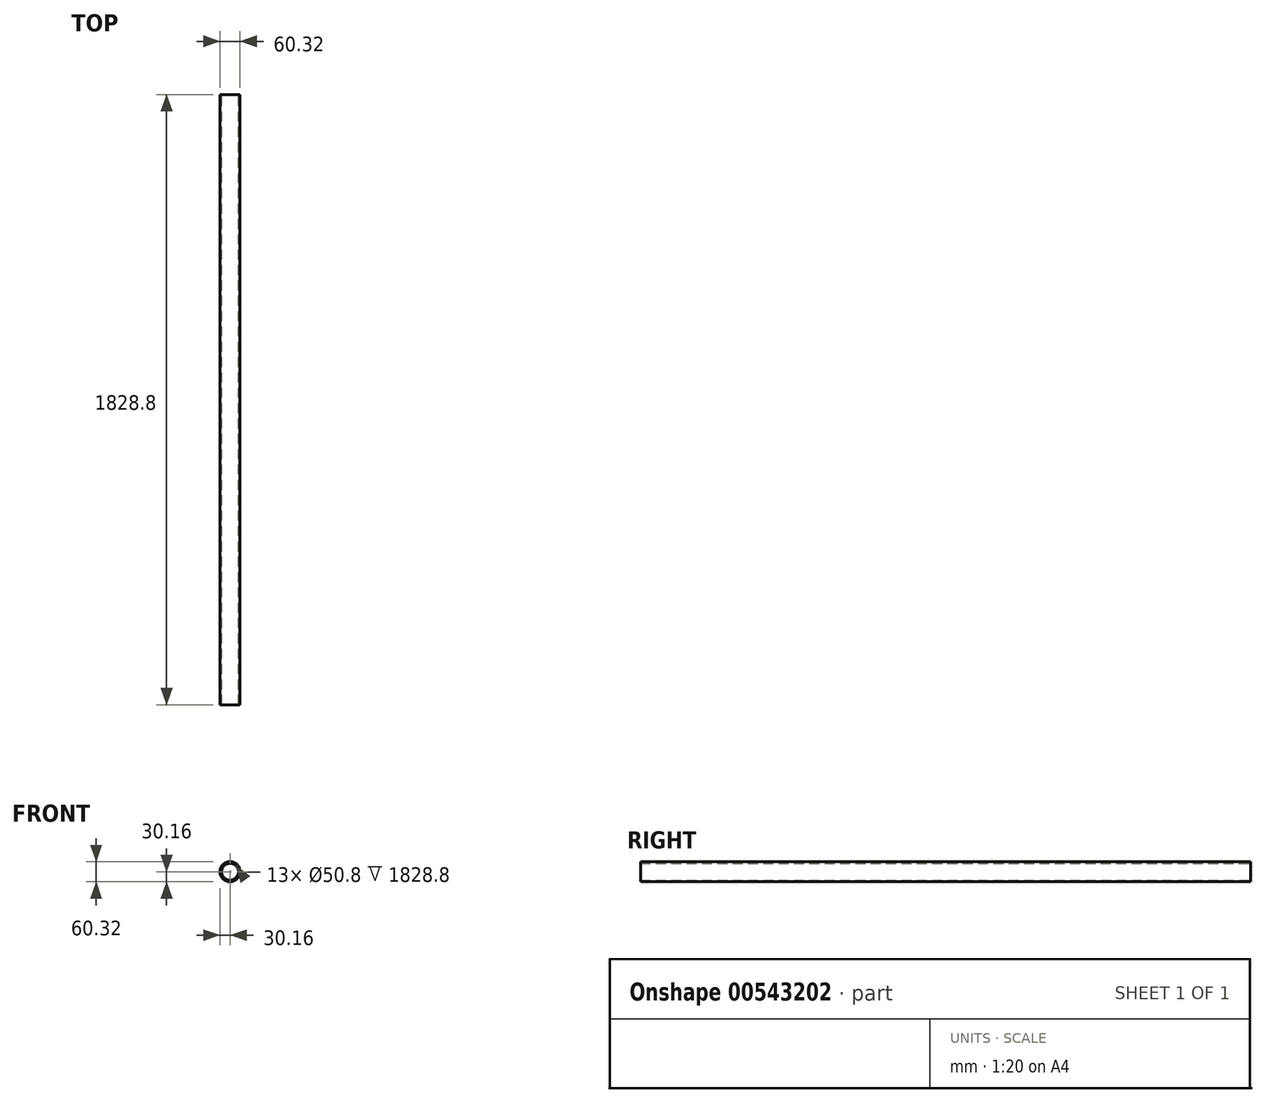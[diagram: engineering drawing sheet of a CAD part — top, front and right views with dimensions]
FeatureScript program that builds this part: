
annotation { "Feature Type Name" : "Feature", "Feature Type Description" : "" }
export const myFeature = defineFeature(function(context is Context, id is Id, definition is map)
    precondition{}
    {
        {
            var Q0;
            Q0=qCreatedBy(makeId("Front.planeOp"),FACE);
            var sketch = newSketch(context, id + "F0", { "sketchPlane" : qUnion([Q0])});
            skCircle(sketch, "E0", {"center": v(0, 0) * mm, "radius": 30.16 * mm});
            skCircle(sketch, "E1", {"center": v(0, 0) * mm, "radius": 25.4 * mm});
            skSolve(sketch);
        }
        {
            var Q0;
            Q0 = qSketchRegion(id + "F0", true);
            extrude(context, id + "F1", {"entities" : qUnion([Q0]), "depth" : 1828.8 * mm, "offsetDistance" : 25.4 * mm});
        }
    });
